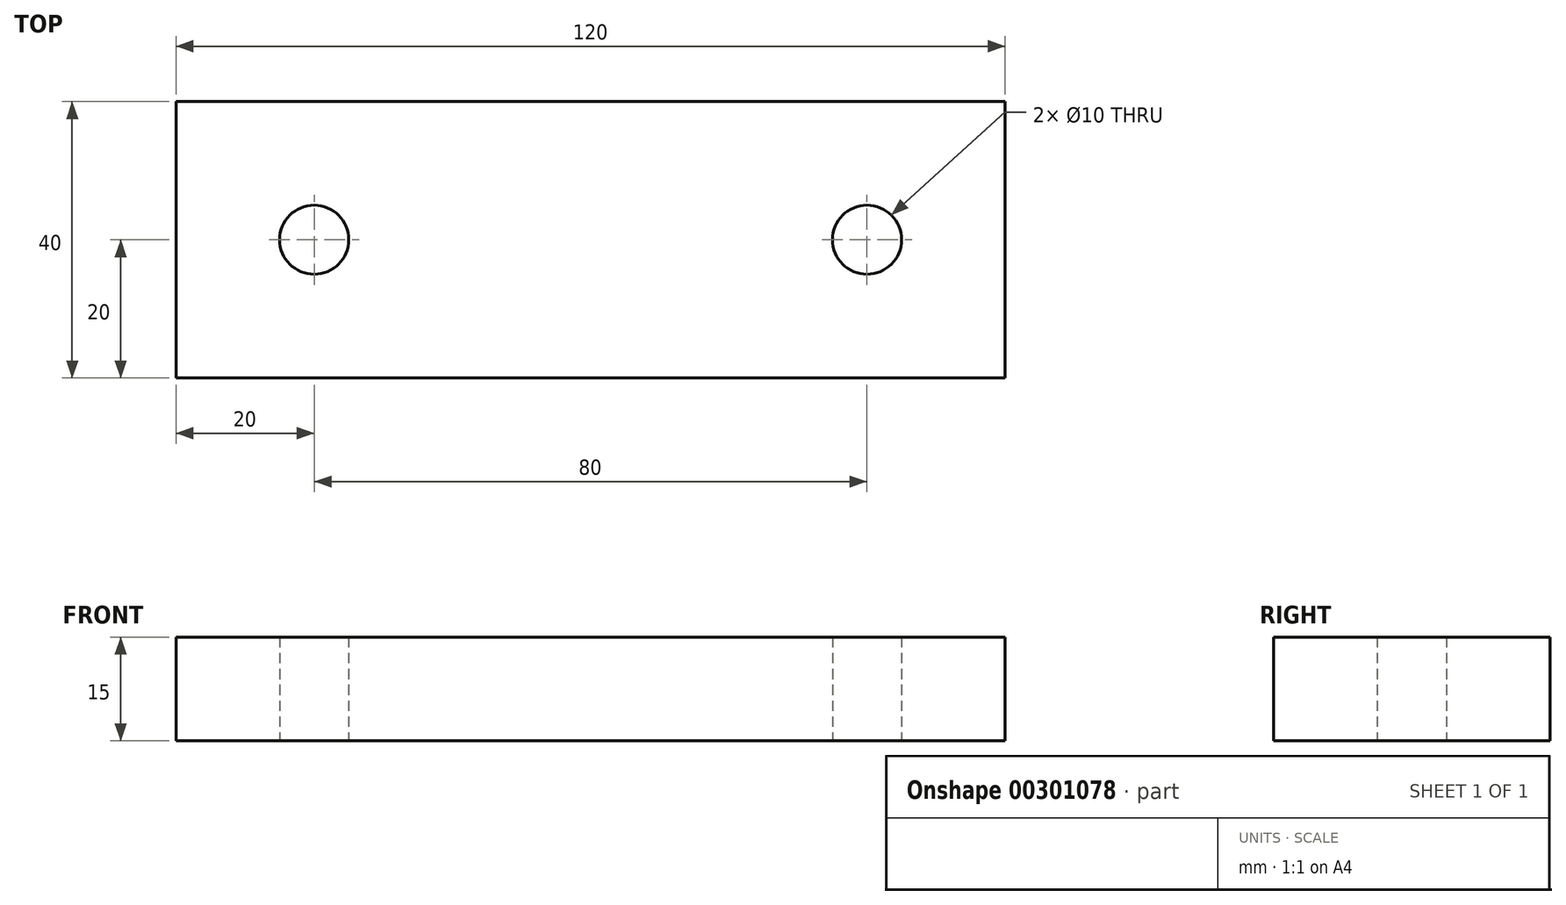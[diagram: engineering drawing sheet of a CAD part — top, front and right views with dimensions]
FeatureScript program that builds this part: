
annotation { "Feature Type Name" : "Feature", "Feature Type Description" : "" }
export const myFeature = defineFeature(function(context is Context, id is Id, definition is map)
    precondition{}
    {
        {
            var Q0;
            Q0=qCreatedBy(makeId("Top.planeOp"),FACE);
            var sketch = newSketch(context, id + "F0", { "sketchPlane" : qUnion([Q0])});
            skLineSegment(sketch, "E0.bottom", {"start": v(0, 0) * mm, "end": v(120, 0) * mm});
            skLineSegment(sketch, "E0.top", {"start": v(0, 40) * mm, "end": v(120, 40) * mm});
            skLineSegment(sketch, "E0.left", {"start": v(0, 0) * mm, "end": v(0, 40) * mm});
            skLineSegment(sketch, "E0.right", {"start": v(120, 0) * mm, "end": v(120, 40) * mm});
            skLineSegment(sketch, "E1", {"start": v(0, 20) * mm, "end": v(120, 20) * mm, "construction": true});
            skCircle(sketch, "E2", {"center": v(20, 20) * mm, "radius": 5 * mm});
            skCircle(sketch, "E3", {"center": v(100, 20) * mm, "radius": 5 * mm});
            skSolve(sketch);
        }
        {
            var Q0;
            Q0=makeQuery(id+"F0.imprint","IMPRINT",FACE,{"disambiguationData":[TD([[makeQuery(id+"F0.imprint","IMPRINT",EDGE,{"derivedFrom":sQuery(id+"F0.wireOp",EDGE,"E0.bottom")}),1.0]])]});
            extrude(context, id + "F1", {"entities" : qUnion([Q0]), "depth" : 15 * mm});
        }
    });
